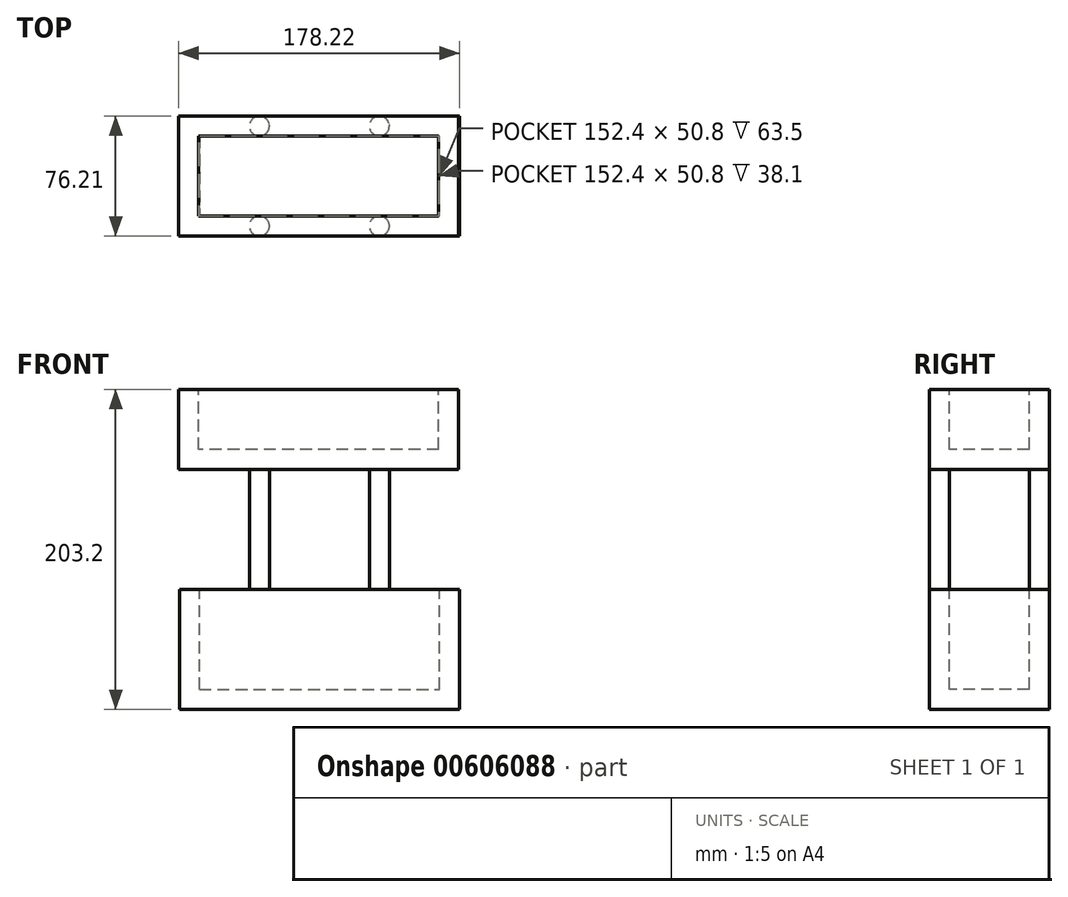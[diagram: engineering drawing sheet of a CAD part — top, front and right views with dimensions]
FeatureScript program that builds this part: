
annotation { "Feature Type Name" : "Feature", "Feature Type Description" : "" }
export const myFeature = defineFeature(function(context is Context, id is Id, definition is map)
    precondition{}
    {
        {
            var Q0;
            Q0=qCreatedBy(makeId("Front.planeOp"),FACE);
            var sketch = newSketch(context, id + "F0", { "sketchPlane" : qUnion([Q0])});
            skLineSegment(sketch, "E0.bottom", {"start": v(-74.55, -72.52) * mm, "end": v(103.25, -72.52) * mm});
            skLineSegment(sketch, "E0.top", {"start": v(-74.55, 3.68) * mm, "end": v(103.25, 3.68) * mm});
            skLineSegment(sketch, "E0.left", {"start": v(-74.55, -72.52) * mm, "end": v(-74.55, 3.68) * mm});
            skLineSegment(sketch, "E0.right", {"start": v(103.25, -72.52) * mm, "end": v(103.25, 3.68) * mm});
            skLineSegment(sketch, "E1", {"start": v(-74.55, 3.68) * mm, "end": v(-49.15, 3.68) * mm});
            skSolve(sketch);
        }
        {
            var Q0;
            Q0 = qSketchRegion(id + "F0", true);
            extrude(context, id + "F1", {"entities" : qUnion([Q0]), "depth" : 76.2 * mm, "offsetDistance" : 25.4 * mm});
        }
        {
            var Q0;
            Q0=makeQuery(id+"F1.opExtrude","SWEPT_FACE",FACE,{"disambiguationData":[OSD([sQuery(id+"F0.wireOp",EDGE,"E0.top")])]});
            var sketch = newSketch(context, id + "F2", { "sketchPlane" : qUnion([Q0])});
            skLineSegment(sketch, "E2", {"start": v(-61.85, -12.7) * mm, "end": v(-61.85, -63.5) * mm});
            skLineSegment(sketch, "E3", {"start": v(-61.85, -63.5) * mm, "end": v(90.55, -63.5) * mm});
            skLineSegment(sketch, "E4", {"start": v(90.55, -63.5) * mm, "end": v(90.55, -12.7) * mm});
            skLineSegment(sketch, "E5", {"start": v(90.55, -12.7) * mm, "end": v(-61.85, -12.7) * mm});
            skLineSegment(sketch, "E6", {"start": v(-61.85, -63.5) * mm, "end": v(-23.75, -63.5) * mm});
            skLineSegment(sketch, "E7", {"start": v(90.55, -63.5) * mm, "end": v(52.45, -63.5) * mm});
            skLineSegment(sketch, "E8", {"start": v(-23.75, -63.5) * mm, "end": v(-23.75, -69.85) * mm});
            skCircle(sketch, "E9", {"center": v(-23.75, -69.85) * mm, "radius": 6.35 * mm});
            skLineSegment(sketch, "E10", {"start": v(-23.75, 0) * mm, "end": v(-23.75, -6.35) * mm});
            skCircle(sketch, "E11", {"center": v(-23.75, -6.35) * mm, "radius": 6.35 * mm});
            skLineSegment(sketch, "E12", {"start": v(52.45, -63.5) * mm, "end": v(52.45, -69.85) * mm});
            skLineSegment(sketch, "E13", {"start": v(52.45, -12.7) * mm, "end": v(52.45, -6.35) * mm});
            skCircle(sketch, "E14", {"center": v(52.45, -6.35) * mm, "radius": 6.35 * mm});
            skCircle(sketch, "E15", {"center": v(52.45, -69.85) * mm, "radius": 6.35 * mm});
            skSolve(sketch);
        }
        {
            var Q0;
            Q0=makeQuery(id+"F2.imprint","IMPRINT",FACE,{"disambiguationData":[TD([[makeQuery(id+"F2.imprint","IMPRINT",EDGE,{"derivedFrom":sQuery(id+"F2.wireOp",EDGE,"E2")}),1.0]])]});
            extrude(context, id + "F3", {"entities" : qUnion([Q0]), "operationType" : NewBodyOperationType.REMOVE, "oppositeDirection" : true, "depth" : 63.5 * mm, "offsetDistance" : 25.4 * mm});
        }
        {
            var Q0;
            Q0 = qSketchRegion(id + "F2", true);
            extrude(context, id + "F4", {"entities" : qUnion([Q0]), "operationType" : NewBodyOperationType.ADD, "depth" : 76.2 * mm, "offsetDistance" : 25.4 * mm});
        }
        {
            var Q0;
            Q0=makeQuery(id+"F4.opExtrude","CAP_FACE",FACE,{"disambiguationData":[OSD([sQuery(id+"F2.wireOp",EDGE,"E2"),sQuery(id+"F2.wireOp",EDGE,"E3"),sQuery(id+"F2.wireOp",EDGE,"E4"),sQuery(id+"F2.wireOp",EDGE,"E5"),sQuery(id+"F2.wireOp",EDGE,"E6"),sQuery(id+"F2.wireOp",EDGE,"E7")])],"isStart":false});
            var sketch = newSketch(context, id + "F5", { "sketchPlane" : qUnion([Q0])});
            skSolve(sketch);
        }
        {
            var Q0;
            Q0 = qSketchRegion(id + "F5", true);
            var Q1;
            Q1=makeQuery(id+"F5.imprint","IMPRINT",FACE,{"disambiguationData":[TD([[makeQuery(id+"F5.imprint","IMPRINT",EDGE,{"derivedFrom":makeQuery(id+"F4.opExtrude","CAP_EDGE",EDGE,{"disambiguationData":[OSD([sQuery(id+"F2.wireOp",EDGE,"E2")])],"isStart":false})}),1.0]])]});
            extrude(context, id + "F6", {"entities" : qUnion([Q0, Q1]), "operationType" : NewBodyOperationType.REMOVE, "oppositeDirection" : true, "depth" : 127 * mm, "offsetDistance" : 25.4 * mm});
        }
        {
            var Q0;
            Q0=makeQuery(id+"F4.opExtrude","CAP_FACE",FACE,{"disambiguationData":[OSD([sQuery(id+"F2.wireOp",EDGE,"E11")])],"isStart":false});
            var sketch = newSketch(context, id + "F7", { "sketchPlane" : qUnion([Q0])});
            skLineSegment(sketch, "E16", {"start": v(-24.17, -0.01) * mm, "end": v(-74.97, -0.01) * mm});
            skLineSegment(sketch, "E17", {"start": v(-74.97, -0.01) * mm, "end": v(-74.97, -76.21) * mm});
            skLineSegment(sketch, "E18", {"start": v(-74.97, -76.21) * mm, "end": v(102.83, -76.21) * mm});
            skLineSegment(sketch, "E19", {"start": v(102.83, -76.21) * mm, "end": v(102.83, 0) * mm});
            skLineSegment(sketch, "E20", {"start": v(102.83, 0) * mm, "end": v(-24.17, -0.01) * mm});
            skSolve(sketch);
        }
        {
            var Q0;
            Q0 = qSketchRegion(id + "F7", true);
            extrude(context, id + "F8", {"entities" : qUnion([Q0]), "operationType" : NewBodyOperationType.ADD, "depth" : 50.8 * mm, "offsetDistance" : 25.4 * mm});
        }
        {
            var Q0;
            Q0=makeQuery(id+"F8.opExtrude","CAP_FACE",FACE,{"disambiguationData":[OSD([sQuery(id+"F7.wireOp",EDGE,"E16"),sQuery(id+"F7.wireOp",EDGE,"E17"),sQuery(id+"F7.wireOp",EDGE,"E18"),sQuery(id+"F7.wireOp",EDGE,"E19"),sQuery(id+"F7.wireOp",EDGE,"E20")])],"isStart":false});
            var sketch = newSketch(context, id + "F9", { "sketchPlane" : qUnion([Q0])});
            skLineSegment(sketch, "E21", {"start": v(-74.97, -0.01) * mm, "end": v(-74.97, -12.71) * mm});
            skLineSegment(sketch, "E22", {"start": v(-74.97, -12.71) * mm, "end": v(-62.27, -12.71) * mm});
            skLineSegment(sketch, "E23", {"start": v(-62.27, -12.71) * mm, "end": v(-62.27, -63.51) * mm});
            skLineSegment(sketch, "E24", {"start": v(-62.27, -63.51) * mm, "end": v(90.13, -63.51) * mm});
            skLineSegment(sketch, "E25", {"start": v(90.13, -63.51) * mm, "end": v(90.13, -12.71) * mm});
            skLineSegment(sketch, "E26", {"start": v(90.13, -12.71) * mm, "end": v(-62.27, -12.71) * mm});
            skSolve(sketch);
        }
        {
            var Q0;
            Q0 = qSketchRegion(id + "F9", true);
            extrude(context, id + "F10", {"entities" : qUnion([Q0]), "operationType" : NewBodyOperationType.REMOVE, "oppositeDirection" : true, "depth" : 38.1 * mm, "offsetDistance" : 25.4 * mm});
        }
    });
